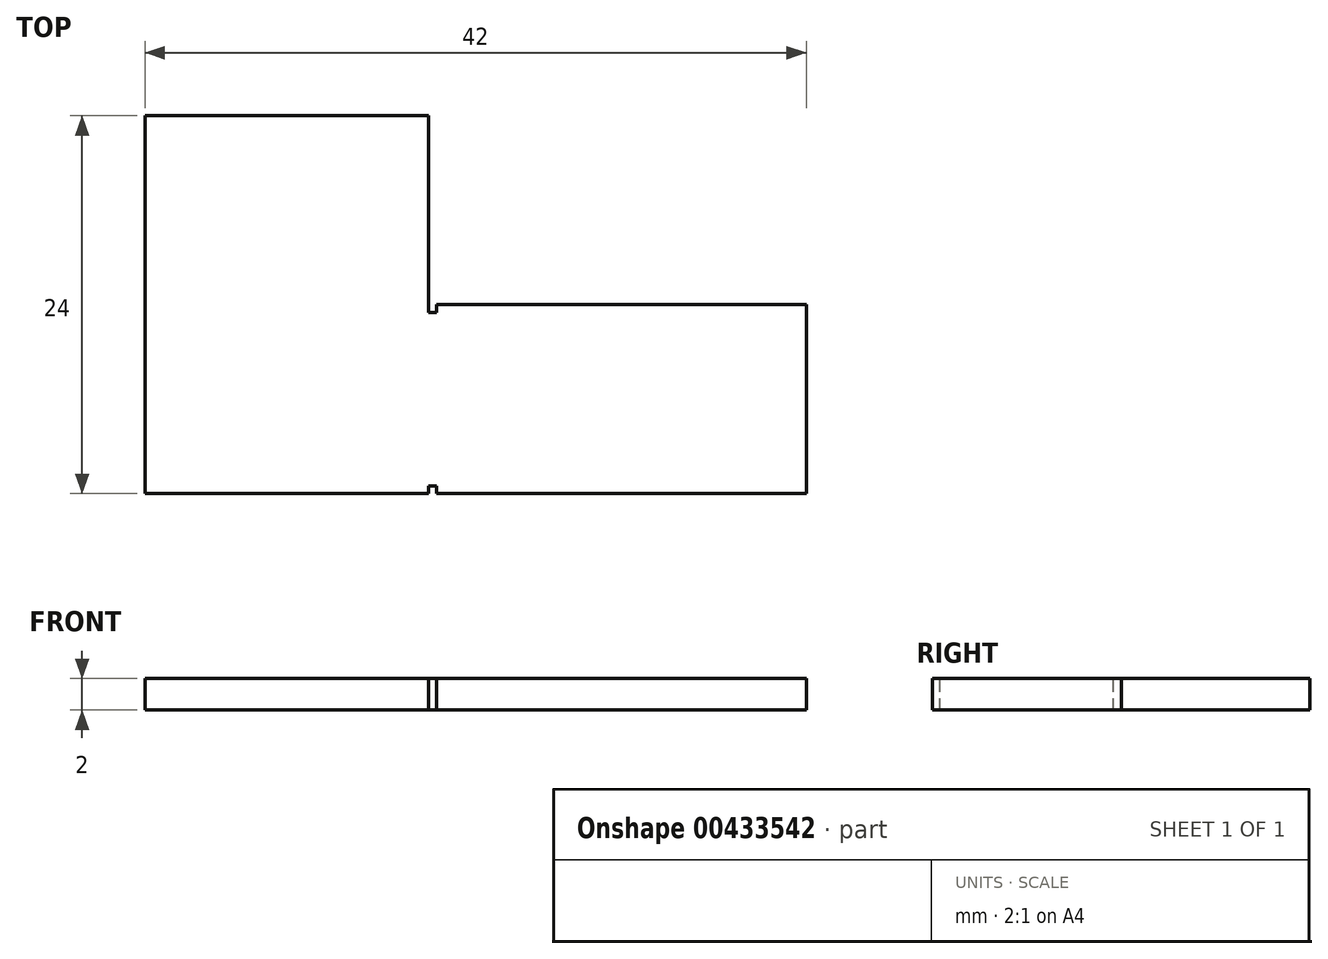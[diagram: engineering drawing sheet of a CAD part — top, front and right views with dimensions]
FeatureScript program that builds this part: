
annotation { "Feature Type Name" : "Feature", "Feature Type Description" : "" }
export const myFeature = defineFeature(function(context is Context, id is Id, definition is map)
    precondition{}
    {
        {
            var Q0;
            Q0=qCreatedBy(makeId("Top.planeOp"),FACE);
            var sketch = newSketch(context, id + "F0", { "sketchPlane" : qUnion([Q0])});
            skLineSegment(sketch, "E0.bottom", {"start": v(12, -6) * mm, "end": v(-12, -6) * mm});
            skLineSegment(sketch, "E0.top", {"start": v(12, 6) * mm, "end": v(-12, 6) * mm});
            skLineSegment(sketch, "E0.left", {"start": v(12, -6) * mm, "end": v(12, 6) * mm});
            skPoint(sketch, "E0.middle", {"position": v(0, 0) * mm});
            skLineSegment(sketch, "E1.bottom", {"start": v(-12, -6) * mm, "end": v(-30, -6) * mm});
            skLineSegment(sketch, "E1.top", {"start": v(-12, 18) * mm, "end": v(-30, 18) * mm});
            skLineSegment(sketch, "E1.left", {"start": v(-12, 6) * mm, "end": v(-12, 18) * mm});
            skLineSegment(sketch, "E1.right", {"start": v(-30, -6) * mm, "end": v(-30, 18) * mm});
            skSolve(sketch);
        }
        {
            var Q0;
            Q0=makeQuery(id+"F0.imprint","IMPRINT",FACE,{"disambiguationData":[TD([[makeQuery(id+"F0.imprint","IMPRINT",EDGE,{"derivedFrom":sQuery(id+"F0.wireOp",EDGE,"E0.bottom")}),-1.0]])]});
            var sketch = newSketch(context, id + "F1", { "sketchPlane" : qUnion([Q0])});
            skSolve(sketch);
        }
        {
            var Q0;
            Q0 = qSketchRegion(id + "F1", true);
            var Q1;
            Q1=makeQuery(id+"F0.imprint","IMPRINT",FACE,{"disambiguationData":[TD([[makeQuery(id+"F0.imprint","IMPRINT",EDGE,{"derivedFrom":sQuery(id+"F0.wireOp",EDGE,"E0.bottom")}),-1.0]])]});
            extrude(context, id + "F2", {"entities" : qUnion([Q0, Q1]), "depth" : 2 * mm});
        }
        {
            var Q0;
            Q0=makeQuery(id+"F2.opExtrude","CAP_FACE",FACE,{"disambiguationData":[OSD([sQuery(id+"F0.wireOp",EDGE,"E0.bottom"),sQuery(id+"F0.wireOp",EDGE,"E0.top"),sQuery(id+"F0.wireOp",EDGE,"E0.left"),sQuery(id+"F0.wireOp",EDGE,"E1.bottom"),sQuery(id+"F0.wireOp",EDGE,"E1.top"),sQuery(id+"F0.wireOp",EDGE,"E1.left"),sQuery(id+"F0.wireOp",EDGE,"E1.right")])],"isStart":false});
            var sketch = newSketch(context, id + "F3", { "sketchPlane" : qUnion([Q0])});
            skLineSegment(sketch, "E2.bottom", {"start": v(-12, 6) * mm, "end": v(-11.5, 6) * mm});
            skLineSegment(sketch, "E2.top", {"start": v(-12, 5.5) * mm, "end": v(-11.5, 5.5) * mm});
            skLineSegment(sketch, "E2.left", {"start": v(-12, 6) * mm, "end": v(-12, 5.5) * mm});
            skLineSegment(sketch, "E2.right", {"start": v(-11.5, 6) * mm, "end": v(-11.5, 5.5) * mm});
            skLineSegment(sketch, "E3", {"start": v(-12, 6) * mm, "end": v(-12, -6) * mm});
            skLineSegment(sketch, "E4.bottom", {"start": v(-12, -6) * mm, "end": v(-11.5, -6) * mm});
            skLineSegment(sketch, "E4.top", {"start": v(-12, -5.5) * mm, "end": v(-11.5, -5.5) * mm});
            skLineSegment(sketch, "E4.left", {"start": v(-12, -6) * mm, "end": v(-12, -5.5) * mm});
            skLineSegment(sketch, "E4.right", {"start": v(-11.5, -6) * mm, "end": v(-11.5, -5.5) * mm});
            skSolve(sketch);
        }
        {
            var Q0;
            Q0=makeQuery(id+"F3.imprint","IMPRINT",FACE,{"disambiguationData":[TD([[makeQuery(id+"F3.imprint","IMPRINT",EDGE,{"derivedFrom":sQuery(id+"F3.wireOp",EDGE,"E4.bottom")}),-1.0]])]});
            var Q1;
            {var subQ0=sQuery(id+"F3.wireOp",EDGE,"E2.bottom");Q1=makeQuery(id+"F3.imprint","IMPRINT",FACE,{"disambiguationData":[TD([[makeQuery(id+"F3.imprint","IMPRINT",EDGE,{"derivedFrom":subQ0}),1.0]])]});}
            extrude(context, id + "F4", {"entities" : qUnion([Q0, Q1]), "operationType" : NewBodyOperationType.REMOVE, "endBound" : BoundingType.UP_TO_NEXT, "oppositeDirection" : true, "depth" : 25 * mm});
        }
    });
